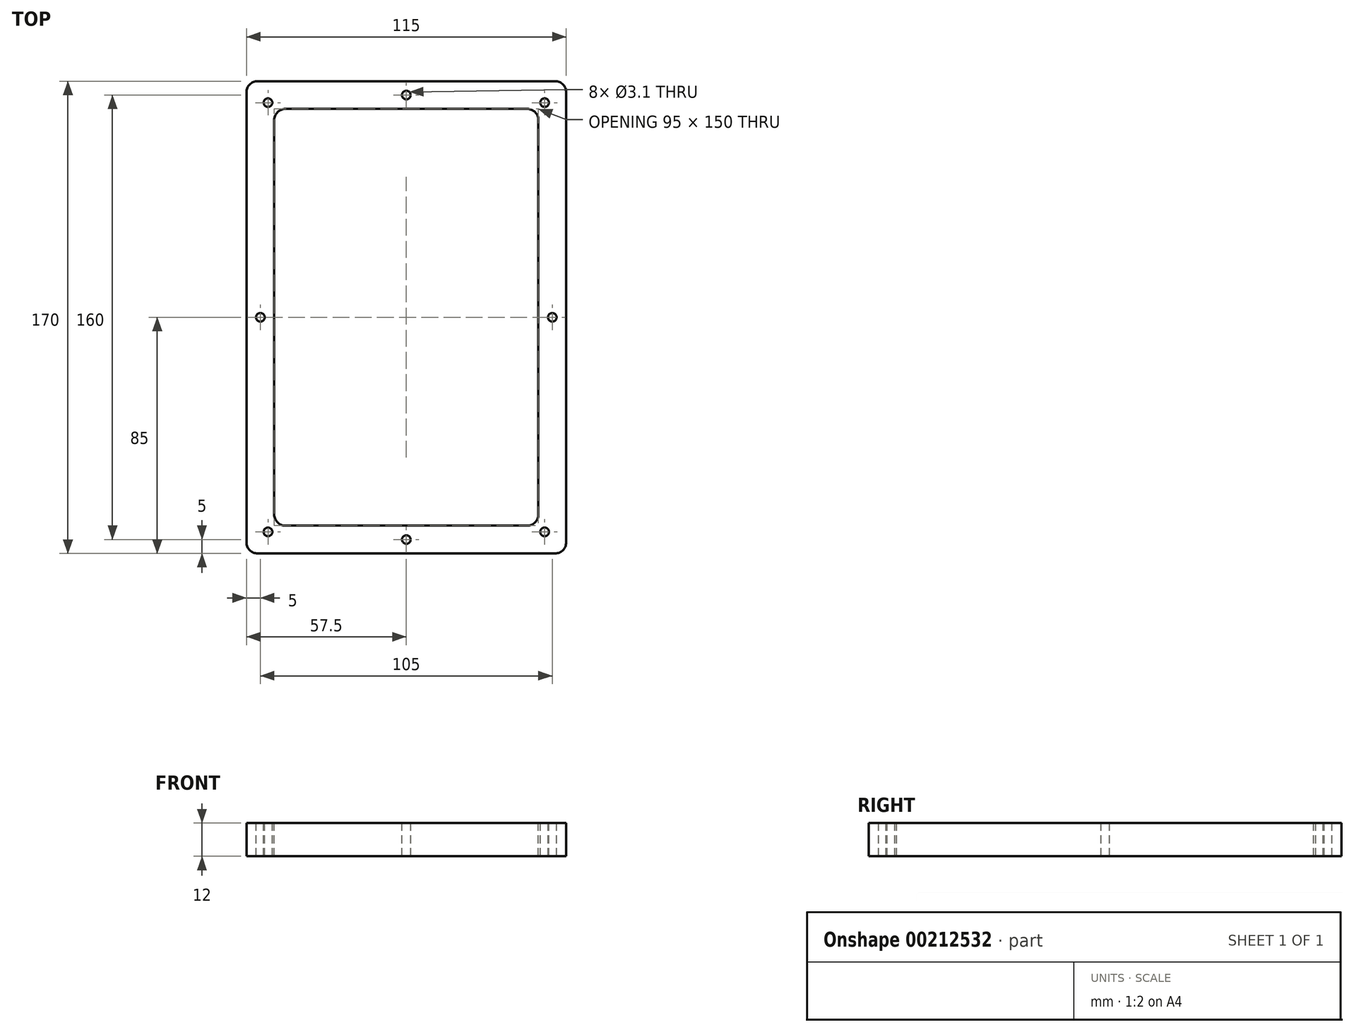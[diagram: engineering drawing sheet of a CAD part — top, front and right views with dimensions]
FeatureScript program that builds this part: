
annotation { "Feature Type Name" : "Feature", "Feature Type Description" : "" }
export const myFeature = defineFeature(function(context is Context, id is Id, definition is map)
    precondition{}
    {
        {
            var Q0;
            Q0=qCreatedBy(makeId("Top.planeOp"),FACE);
            var sketch = newSketch(context, id + "F0", { "sketchPlane" : qUnion([Q0])});
            skLineSegment(sketch, "E0.bottom", {"start": v(-57.5, 85) * mm, "end": v(57.5, 85) * mm});
            skLineSegment(sketch, "E0.top", {"start": v(-57.5, -85) * mm, "end": v(57.5, -85) * mm});
            skLineSegment(sketch, "E0.left", {"start": v(-57.5, 85) * mm, "end": v(-57.5, -85) * mm});
            skLineSegment(sketch, "E0.right", {"start": v(57.5, 85) * mm, "end": v(57.5, -85) * mm});
            skSolve(sketch);
        }
        {
            var Q0;
            Q0 = qSketchRegion(id + "F0", true);
            extrude(context, id + "F1", {"entities" : qUnion([Q0]), "depth" : 12 * mm});
        }
        {
            var Q0;
            Q0=makeQuery(id+"F1.opExtrude","CAP_FACE",FACE,{"disambiguationData":[OSD([sQuery(id+"F0.wireOp",EDGE,"E0.bottom"),sQuery(id+"F0.wireOp",EDGE,"E0.top"),sQuery(id+"F0.wireOp",EDGE,"E0.left"),sQuery(id+"F0.wireOp",EDGE,"E0.right")])],"isStart":false});
            var sketch = newSketch(context, id + "F2", { "sketchPlane" : qUnion([Q0])});
            skLineSegment(sketch, "E1.bottom", {"start": v(-47.5, 75) * mm, "end": v(47.5, 75) * mm});
            skLineSegment(sketch, "E1.top", {"start": v(-47.5, -75) * mm, "end": v(47.5, -75) * mm});
            skLineSegment(sketch, "E1.left", {"start": v(-47.5, 75) * mm, "end": v(-47.5, -75) * mm});
            skLineSegment(sketch, "E1.right", {"start": v(47.5, 75) * mm, "end": v(47.5, -75) * mm});
            skSolve(sketch);
        }
        {
            var Q0;
            Q0 = qSketchRegion(id + "F2", true);
            extrude(context, id + "F3", {"entities" : qUnion([Q0]), "operationType" : NewBodyOperationType.REMOVE, "endBound" : BoundingType.THROUGH_ALL, "oppositeDirection" : true, "depth" : 25 * mm});
        }
        {
            var Q0;
            Q0=makeQuery(id+"F1.opExtrude","CAP_FACE",FACE,{"disambiguationData":[OSD([sQuery(id+"F0.wireOp",EDGE,"E0.bottom"),sQuery(id+"F0.wireOp",EDGE,"E0.top"),sQuery(id+"F0.wireOp",EDGE,"E0.left"),sQuery(id+"F0.wireOp",EDGE,"E0.right")])],"isStart":false});
            var sketch = newSketch(context, id + "F4", { "sketchPlane" : qUnion([Q0])});
            skCircle(sketch, "E2", {"center": v(0, 80) * mm, "radius": 1.55 * mm});
            skPoint(sketch, "E2.centerSnap0", {"position": v(0, 75) * mm});
            skCircle(sketch, "E3", {"center": v(0, -80) * mm, "radius": 1.55 * mm});
            skPoint(sketch, "E3.centerSnap0", {"position": v(0, -85) * mm});
            skCircle(sketch, "E4", {"center": v(52.5, 0) * mm, "radius": 1.55 * mm});
            skPoint(sketch, "E4.centerSnap0", {"position": v(47.5, 0) * mm});
            skCircle(sketch, "E5", {"center": v(-52.5, 0) * mm, "radius": 1.55 * mm});
            skPoint(sketch, "E5.centerSnap0", {"position": v(-47.5, 0) * mm});
            skLineSegment(sketch, "E6", {"start": v(-47.5, 0) * mm, "end": v(-57.5, 0) * mm, "construction": true});
            skLineSegment(sketch, "E7", {"start": v(47.5, 0) * mm, "end": v(57.5, 0) * mm, "construction": true});
            skLineSegment(sketch, "E8", {"start": v(0, 75) * mm, "end": v(0, 85) * mm, "construction": true});
            skLineSegment(sketch, "E9", {"start": v(0, -75) * mm, "end": v(0, -85) * mm, "construction": true});
            skSolve(sketch);
        }
        {
            var Q0;
            Q0 = qSketchRegion(id + "F4", true);
            extrude(context, id + "F5", {"entities" : qUnion([Q0]), "operationType" : NewBodyOperationType.REMOVE, "endBound" : BoundingType.THROUGH_ALL, "oppositeDirection" : true, "depth" : 25 * mm});
        }
        {
            var Q0;
            Q0=makeQuery(id+"F3.boolean.opBoolean","COPY",EDGE,{"derivedFrom":makeQuery(id+"F3.opExtrude","SWEPT_EDGE",EDGE,{"disambiguationData":[OSD([sQuery(id+"F2.wireOp",EDGE,"E1.bottom"),sQuery(id+"F2.wireOp",EDGE,"E1.right")])]})});
            var Q1;
            Q1=makeQuery(id+"F3.boolean.opBoolean","COPY",EDGE,{"derivedFrom":makeQuery(id+"F3.opExtrude","SWEPT_EDGE",EDGE,{"disambiguationData":[OSD([sQuery(id+"F2.wireOp",EDGE,"E1.bottom"),sQuery(id+"F2.wireOp",EDGE,"E1.left")])]})});
            var Q2;
            Q2=makeQuery(id+"F1.opExtrude","SWEPT_EDGE",EDGE,{"disambiguationData":[OSD([sQuery(id+"F0.wireOp",EDGE,"E0.bottom"),sQuery(id+"F0.wireOp",EDGE,"E0.right")])]});
            var Q3;
            Q3=makeQuery(id+"F1.opExtrude","SWEPT_EDGE",EDGE,{"disambiguationData":[OSD([sQuery(id+"F0.wireOp",EDGE,"E0.top"),sQuery(id+"F0.wireOp",EDGE,"E0.right")])]});
            var Q4;
            Q4=makeQuery(id+"F1.opExtrude","SWEPT_EDGE",EDGE,{"disambiguationData":[OSD([sQuery(id+"F0.wireOp",EDGE,"E0.top"),sQuery(id+"F0.wireOp",EDGE,"E0.left")])]});
            var Q5;
            Q5=makeQuery(id+"F1.opExtrude","SWEPT_EDGE",EDGE,{"disambiguationData":[OSD([sQuery(id+"F0.wireOp",EDGE,"E0.bottom"),sQuery(id+"F0.wireOp",EDGE,"E0.left")])]});
            var Q6;
            Q6=makeQuery(id+"F3.boolean.opBoolean","COPY",EDGE,{"derivedFrom":makeQuery(id+"F3.opExtrude","SWEPT_EDGE",EDGE,{"disambiguationData":[OSD([sQuery(id+"F2.wireOp",EDGE,"E1.top"),sQuery(id+"F2.wireOp",EDGE,"E1.right")])]})});
            var Q7;
            Q7=makeQuery(id+"F3.boolean.opBoolean","COPY",EDGE,{"derivedFrom":makeQuery(id+"F3.opExtrude","SWEPT_EDGE",EDGE,{"disambiguationData":[OSD([sQuery(id+"F2.wireOp",EDGE,"E1.top"),sQuery(id+"F2.wireOp",EDGE,"E1.left")])]})});
            fillet(context, id + "F6", {"entities" : qUnion([Q0, Q1, Q2, Q3, Q4, Q5, Q6, Q7]), "radius" : 4 * mm, "tangentPropagation" : true, "allowEdgeOverflow" : false});
        }
        {
            var Q0;
            Q0=makeQuery(id+"F1.opExtrude","CAP_FACE",FACE,{"disambiguationData":[OSD([sQuery(id+"F0.wireOp",EDGE,"E0.bottom"),sQuery(id+"F0.wireOp",EDGE,"E0.top"),sQuery(id+"F0.wireOp",EDGE,"E0.left"),sQuery(id+"F0.wireOp",EDGE,"E0.right")])],"isStart":false});
            var sketch = newSketch(context, id + "F7", { "sketchPlane" : qUnion([Q0])});
            skCircle(sketch, "E10", {"center": v(-49.75, 77.25) * mm, "radius": 1.55 * mm});
            skCircle(sketch, "E11", {"center": v(49.75, 77.25) * mm, "radius": 1.55 * mm});
            skCircle(sketch, "E12", {"center": v(49.75, -77.25) * mm, "radius": 1.55 * mm});
            skCircle(sketch, "E13", {"center": v(-49.75, -77.25) * mm, "radius": 1.55 * mm});
            skSolve(sketch);
        }
        {
            var Q0;
            Q0 = qSketchRegion(id + "F7", true);
            extrude(context, id + "F8", {"entities" : qUnion([Q0]), "operationType" : NewBodyOperationType.REMOVE, "endBound" : BoundingType.THROUGH_ALL, "oppositeDirection" : true, "depth" : 25 * mm});
        }
    });
